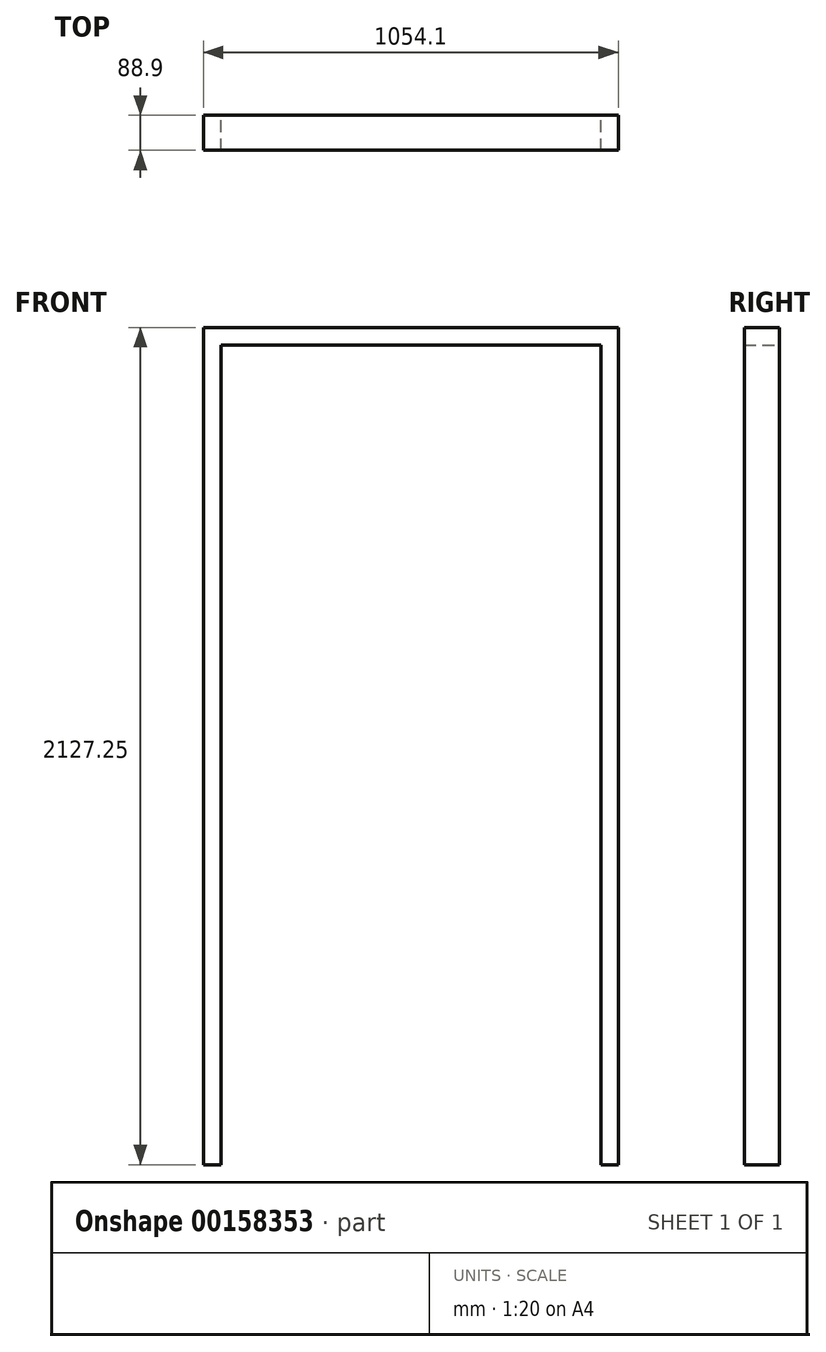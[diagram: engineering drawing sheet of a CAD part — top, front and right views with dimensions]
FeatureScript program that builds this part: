
annotation { "Feature Type Name" : "Feature", "Feature Type Description" : "" }
export const myFeature = defineFeature(function(context is Context, id is Id, definition is map)
    precondition{}
    {
        {
            var Q0;
            Q0=qCreatedBy(makeId("Front.planeOp"),FACE);
            var sketch = newSketch(context, id + "F0", { "sketchPlane" : qUnion([Q0])});
            skLineSegment(sketch, "E0", {"start": v(44.45, -774.95) * mm, "end": v(44.45, 1307.85) * mm});
            skLineSegment(sketch, "E1", {"start": v(44.45, 1307.85) * mm, "end": v(1009.65, 1307.85) * mm});
            skLineSegment(sketch, "E2", {"start": v(1009.65, 1307.85) * mm, "end": v(1009.65, -774.95) * mm});
            skLineSegment(sketch, "E3", {"start": v(1009.65, -774.95) * mm, "end": v(1054.1, -774.95) * mm});
            skLineSegment(sketch, "E4", {"start": v(1054.1, -774.95) * mm, "end": v(1054.1, 1352.3) * mm});
            skLineSegment(sketch, "E5", {"start": v(1054.1, 1352.3) * mm, "end": v(0, 1352.3) * mm});
            skLineSegment(sketch, "E6", {"start": v(0, 1352.3) * mm, "end": v(0, -774.95) * mm});
            skLineSegment(sketch, "E7", {"start": v(0, -774.95) * mm, "end": v(44.45, -774.95) * mm});
            skLineSegment(sketch, "E8", {"start": v(1009.65, 1307.85) * mm, "end": v(1054.1, 1307.85) * mm});
            skLineSegment(sketch, "E9", {"start": v(44.45, 1307.85) * mm, "end": v(0, 1307.85) * mm});
            skLineSegment(sketch, "E10", {"start": v(527.05, 1352.3) * mm, "end": v(527.05, 1663.45) * mm});
            skSolve(sketch);
        }
        {
            var Q0;
            Q0=makeQuery(id+"F0.imprint","IMPRINT",FACE,{"disambiguationData":[TD([[makeQuery(id+"F0.imprint","IMPRINT",EDGE,{"derivedFrom":sQuery(id+"F0.wireOp",EDGE,"E2")}),1.0]])]});
            var Q1;
            Q1=makeQuery(id+"F0.imprint","IMPRINT",FACE,{"disambiguationData":[TD([[makeQuery(id+"F0.imprint","IMPRINT",EDGE,{"derivedFrom":sQuery(id+"F0.wireOp",EDGE,"E0")}),1.0]])]});
            var Q2;
            Q2=makeQuery(id+"F0.imprint","IMPRINT",FACE,{"disambiguationData":[TD([[makeQuery(id+"F0.imprint","IMPRINT",EDGE,{"derivedFrom":sQuery(id+"F0.wireOp",EDGE,"E1")}),1.0]])]});
            extrude(context, id + "F1", {"entities" : qUnion([Q0, Q1, Q2]), "endBound" : BoundingType.SYMMETRIC, "depth" : 88.9 * mm});
        }
    });
